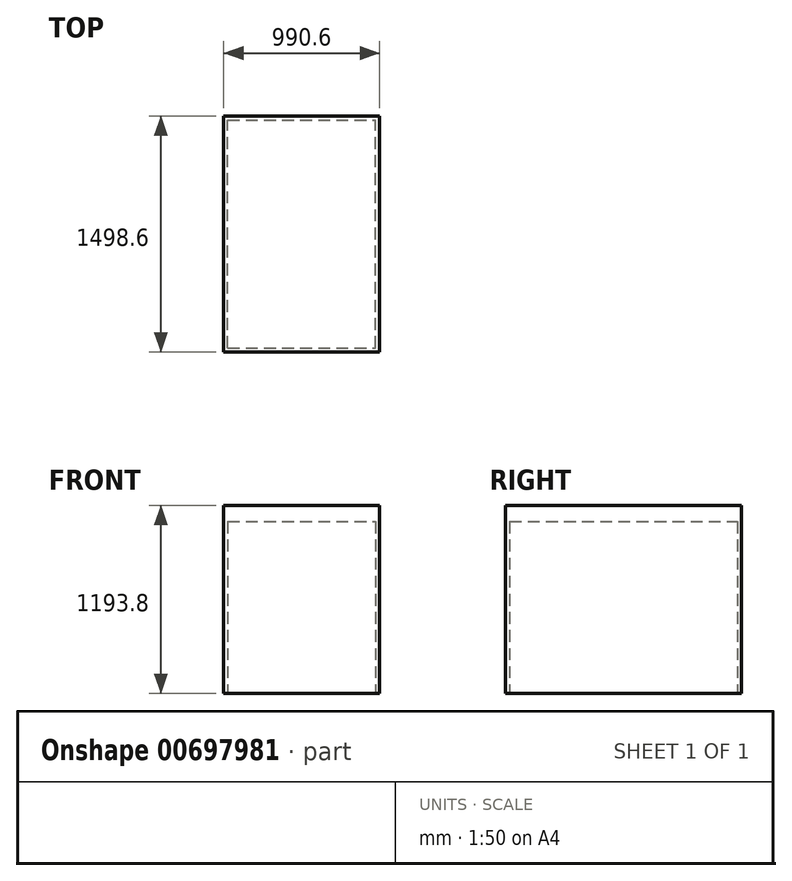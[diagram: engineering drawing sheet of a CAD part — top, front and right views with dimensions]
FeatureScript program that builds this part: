
annotation { "Feature Type Name" : "Feature", "Feature Type Description" : "" }
export const myFeature = defineFeature(function(context is Context, id is Id, definition is map)
    precondition{}
    {
        {
            var Q0;
            Q0=qCreatedBy(makeId("Top.planeOp"),FACE);
            var sketch = newSketch(context, id + "F0", { "sketchPlane" : qUnion([Q0])});
            skLineSegment(sketch, "E0.bottom", {"start": v(495.3, -749.3) * mm, "end": v(-495.3, -749.3) * mm});
            skLineSegment(sketch, "E0.top", {"start": v(495.3, 749.3) * mm, "end": v(-495.3, 749.3) * mm});
            skLineSegment(sketch, "E0.left", {"start": v(495.3, -749.3) * mm, "end": v(495.3, 749.3) * mm});
            skLineSegment(sketch, "E0.right", {"start": v(-495.3, -749.3) * mm, "end": v(-495.3, 749.3) * mm});
            skPoint(sketch, "E0.middle", {"position": v(0, 0) * mm});
            skSolve(sketch);
        }
        {
            var Q0;
            Q0 = qSketchRegion(id + "F0", true);
            extrude(context, id + "F1", {"entities" : qUnion([Q0]), "depth" : 1193.8 * mm, "offsetDistance" : 25.4 * mm});
        }
        {
            var Q0;
            Q0=makeQuery(id+"F1.opExtrude","CAP_FACE",FACE,{"disambiguationData":[OSD([sQuery(id+"F0.wireOp",EDGE,"E0.bottom"),sQuery(id+"F0.wireOp",EDGE,"E0.top"),sQuery(id+"F0.wireOp",EDGE,"E0.left"),sQuery(id+"F0.wireOp",EDGE,"E0.right")])],"isStart":true});
            var sketch = newSketch(context, id + "F2", { "sketchPlane" : qUnion([Q0])});
            skLineSegment(sketch, "E1.bottom", {"start": v(-469.9, 723.9) * mm, "end": v(469.9, 723.9) * mm});
            skLineSegment(sketch, "E1.top", {"start": v(-469.9, -723.9) * mm, "end": v(469.9, -723.9) * mm});
            skLineSegment(sketch, "E1.left", {"start": v(-469.9, 723.9) * mm, "end": v(-469.9, -723.9) * mm});
            skLineSegment(sketch, "E1.right", {"start": v(469.9, 723.9) * mm, "end": v(469.9, -723.9) * mm});
            skPoint(sketch, "E1.middle", {"position": v(0, 0) * mm});
            skSolve(sketch);
        }
        {
            var Q0;
            Q0=makeQuery(id+"F2.imprint","IMPRINT",FACE,{"disambiguationData":[TD([[makeQuery(id+"F2.imprint","IMPRINT",EDGE,{"derivedFrom":sQuery(id+"F2.wireOp",EDGE,"E1.bottom")}),-1.0]])]});
            extrude(context, id + "F3", {"entities" : qUnion([Q0]), "operationType" : NewBodyOperationType.REMOVE, "oppositeDirection" : true, "depth" : 1092.2 * mm, "offsetDistance" : 25.4 * mm});
        }
    });
